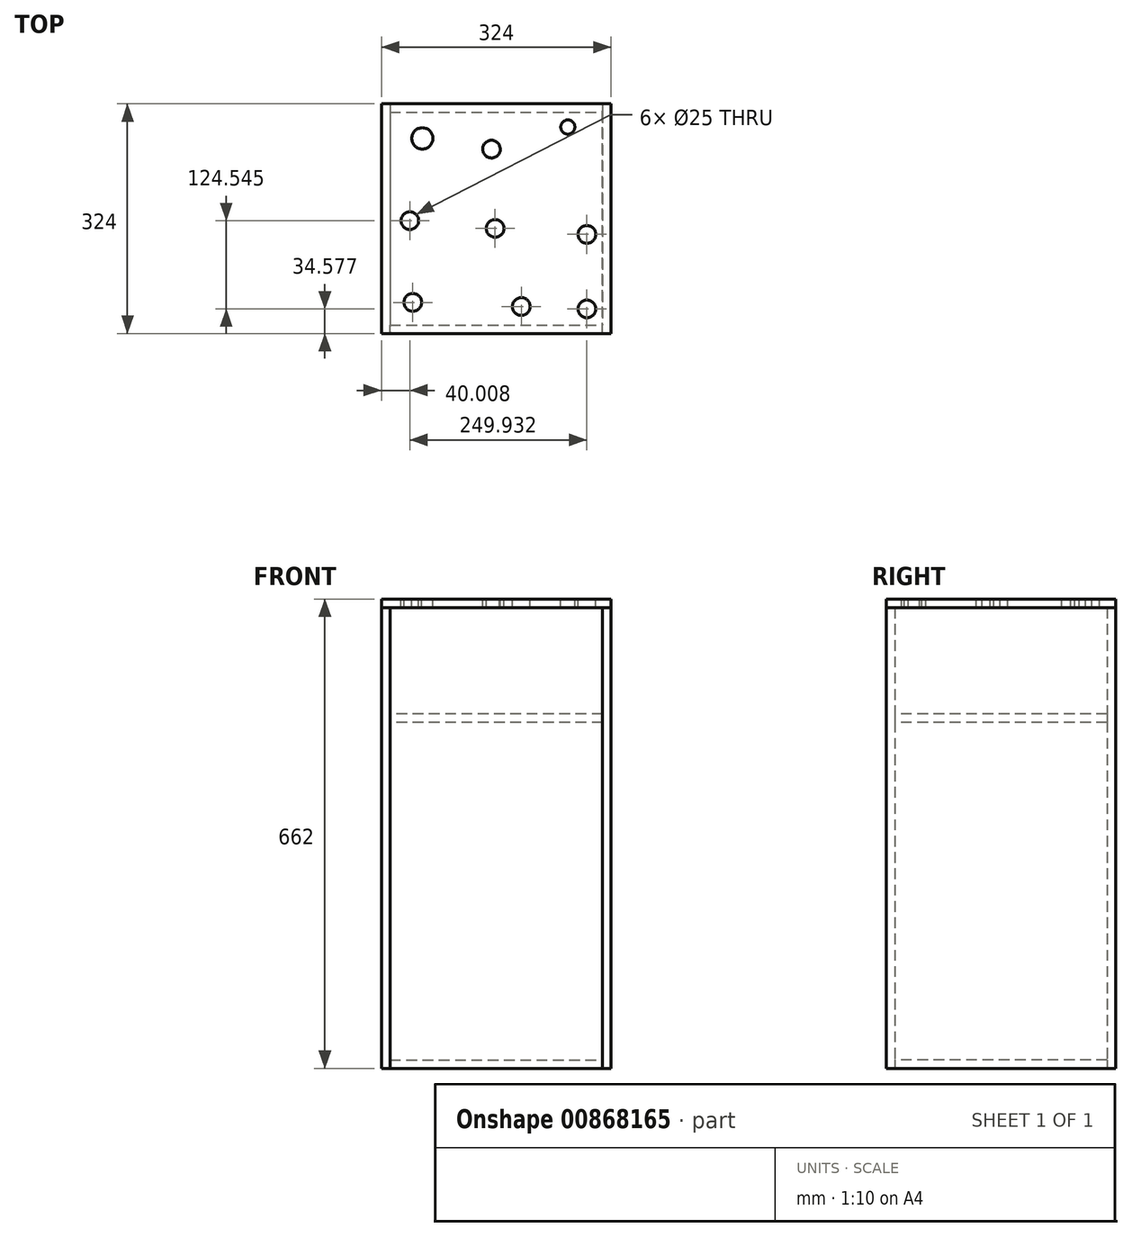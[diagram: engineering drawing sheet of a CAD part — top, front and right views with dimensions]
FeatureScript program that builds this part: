
annotation { "Feature Type Name" : "Feature", "Feature Type Description" : "" }
export const myFeature = defineFeature(function(context is Context, id is Id, definition is map)
    precondition{}
    {
        {
            var Q0;
            Q0=qCreatedBy(makeId("Top.planeOp"),FACE);
            var sketch = newSketch(context, id + "F0", { "sketchPlane" : qUnion([Q0])});
            skLineSegment(sketch, "E0.bottom", {"start": v(-158.95, 142.22) * mm, "end": v(141.05, 142.22) * mm});
            skLineSegment(sketch, "E0.top", {"start": v(-158.95, -157.78) * mm, "end": v(141.05, -157.78) * mm});
            skLineSegment(sketch, "E0.left", {"start": v(-158.95, 142.22) * mm, "end": v(-158.95, -157.78) * mm});
            skLineSegment(sketch, "E0.right", {"start": v(141.05, 142.22) * mm, "end": v(141.05, -157.78) * mm});
            skSolve(sketch);
        }
        {
            var Q0;
            Q0 = qSketchRegion(id + "F0", true);
            extrude(context, id + "F1", {"entities" : qUnion([Q0]), "depth" : 12 * mm, "offsetDistance" : 25 * mm});
        }
        {
            var Q0;
            Q0=makeQuery(id+"F1.opExtrude","SWEPT_FACE",FACE,{"disambiguationData":[OSD([sQuery(id+"F0.wireOp",EDGE,"E0.top")])]});
            var sketch = newSketch(context, id + "F2", { "sketchPlane" : qUnion([Q0])});
            skLineSegment(sketch, "E1.bottom", {"start": v(-158.95, 0) * mm, "end": v(141.05, 0) * mm});
            skLineSegment(sketch, "E1.top", {"start": v(-158.95, 650) * mm, "end": v(141.05, 650) * mm});
            skLineSegment(sketch, "E1.left", {"start": v(-158.95, 0) * mm, "end": v(-158.95, 650) * mm});
            skLineSegment(sketch, "E1.right", {"start": v(141.05, 0) * mm, "end": v(141.05, 650) * mm});
            skSolve(sketch);
        }
        {
            var Q0;
            Q0 = qSketchRegion(id + "F2", true);
            extrude(context, id + "F3", {"entities" : qUnion([Q0]), "depth" : 12 * mm, "offsetDistance" : 25 * mm});
        }
        {
            var Q0;
            Q0=makeQuery(id+"F1.opExtrude","SWEPT_FACE",FACE,{"disambiguationData":[OSD([sQuery(id+"F0.wireOp",EDGE,"E0.bottom")])]});
            var sketch = newSketch(context, id + "F4", { "sketchPlane" : qUnion([Q0])});
            skLineSegment(sketch, "E2.bottom", {"start": v(-141.05, 0) * mm, "end": v(158.95, 0) * mm});
            skLineSegment(sketch, "E2.top", {"start": v(-141.05, 650) * mm, "end": v(158.95, 650) * mm});
            skLineSegment(sketch, "E2.left", {"start": v(-141.05, 0) * mm, "end": v(-141.05, 650) * mm});
            skLineSegment(sketch, "E2.right", {"start": v(158.95, 0) * mm, "end": v(158.95, 650) * mm});
            skSolve(sketch);
        }
        {
            var Q0;
            Q0 = qSketchRegion(id + "F4", true);
            extrude(context, id + "F5", {"entities" : qUnion([Q0]), "depth" : 12 * mm, "offsetDistance" : 25 * mm});
        }
        {
            var Q0;
            Q0=makeQuery(id+"F3.opExtrude","CAP_FACE",FACE,{"disambiguationData":[OSD([sQuery(id+"F2.wireOp",EDGE,"E1.bottom"),sQuery(id+"F2.wireOp",EDGE,"E1.top"),sQuery(id+"F2.wireOp",EDGE,"E1.left"),sQuery(id+"F2.wireOp",EDGE,"E1.right")])],"isStart":true});
            var sketch = newSketch(context, id + "F6", { "sketchPlane" : qUnion([Q0])});
            skLineSegment(sketch, "E3.bottom", {"start": v(-141.05, 500) * mm, "end": v(158.95, 500) * mm});
            skLineSegment(sketch, "E3.top", {"start": v(-141.05, 488) * mm, "end": v(158.95, 488) * mm});
            skLineSegment(sketch, "E3.left", {"start": v(-141.05, 500) * mm, "end": v(-141.05, 488) * mm});
            skLineSegment(sketch, "E3.right", {"start": v(158.95, 500) * mm, "end": v(158.95, 488) * mm});
            skSolve(sketch);
        }
        {
            var Q0;
            Q0 = qSketchRegion(id + "F6", true);
            var Q1;
            Q1=makeQuery(id+"F5.opExtrude","CAP_FACE",FACE,{"disambiguationData":[OSD([sQuery(id+"F4.wireOp",EDGE,"E2.bottom"),sQuery(id+"F4.wireOp",EDGE,"E2.top"),sQuery(id+"F4.wireOp",EDGE,"E2.left"),sQuery(id+"F4.wireOp",EDGE,"E2.right")])],"isStart":true});
            extrude(context, id + "F7", {"entities" : qUnion([Q0]), "endBound" : BoundingType.UP_TO_SURFACE, "depth" : 25 * mm, "endBoundEntityFace" : qUnion([Q1]), "offsetDistance" : 25 * mm});
        }
        {
            var Q0;
            Q0=makeQuery(id+"F3.opExtrude","SWEPT_FACE",FACE,{"disambiguationData":[OSD([sQuery(id+"F2.wireOp",EDGE,"E1.right")])]});
            var sketch = newSketch(context, id + "F8", { "sketchPlane" : qUnion([Q0])});
            skLineSegment(sketch, "E4.bottom", {"start": v(-169.78, 0) * mm, "end": v(154.22, 0) * mm});
            skLineSegment(sketch, "E4.top", {"start": v(-169.78, 650) * mm, "end": v(154.22, 650) * mm});
            skLineSegment(sketch, "E4.left", {"start": v(-169.78, 0) * mm, "end": v(-169.78, 650) * mm});
            skLineSegment(sketch, "E4.right", {"start": v(154.22, 0) * mm, "end": v(154.22, 650) * mm});
            skSolve(sketch);
        }
        {
            var Q0;
            Q0 = qSketchRegion(id + "F8", true);
            extrude(context, id + "F9", {"entities" : qUnion([Q0]), "depth" : 12 * mm, "offsetDistance" : 25 * mm});
        }
        {
            var Q0;
            Q0=makeQuery(id+"F5.opExtrude","SWEPT_FACE",FACE,{"disambiguationData":[OSD([sQuery(id+"F4.wireOp",EDGE,"E2.right")])]});
            var sketch = newSketch(context, id + "F10", { "sketchPlane" : qUnion([Q0])});
            skLineSegment(sketch, "E5.bottom", {"start": v(-154.22, 650) * mm, "end": v(169.78, 650) * mm});
            skLineSegment(sketch, "E5.top", {"start": v(-154.22, 0) * mm, "end": v(169.78, 0) * mm});
            skLineSegment(sketch, "E5.left", {"start": v(-154.22, 650) * mm, "end": v(-154.22, 0) * mm});
            skLineSegment(sketch, "E5.right", {"start": v(169.78, 650) * mm, "end": v(169.78, 0) * mm});
            skSolve(sketch);
        }
        {
            var Q0;
            Q0 = qSketchRegion(id + "F10", true);
            extrude(context, id + "F11", {"entities" : qUnion([Q0]), "depth" : 12 * mm, "offsetDistance" : 25 * mm});
        }
        {
            var Q0;
            Q0=makeQuery(id+"F9.opExtrude","SWEPT_FACE",FACE,{"disambiguationData":[OSD([sQuery(id+"F8.wireOp",EDGE,"E4.top")])]});
            var sketch = newSketch(context, id + "F12", { "sketchPlane" : qUnion([Q0])});
            skLineSegment(sketch, "E6.bottom", {"start": v(153.05, -169.78) * mm, "end": v(-170.95, -169.78) * mm});
            skLineSegment(sketch, "E6.top", {"start": v(153.05, 154.22) * mm, "end": v(-170.95, 154.22) * mm});
            skLineSegment(sketch, "E6.left", {"start": v(153.05, -169.78) * mm, "end": v(153.05, 154.22) * mm});
            skLineSegment(sketch, "E6.right", {"start": v(-170.95, -169.78) * mm, "end": v(-170.95, 154.22) * mm});
            skSolve(sketch);
        }
        {
            var Q0;
            Q0 = qSketchRegion(id + "F12", true);
            extrude(context, id + "F13", {"entities" : qUnion([Q0]), "depth" : 12 * mm, "offsetDistance" : 25 * mm});
        }
        {
            var Q0;
            Q0=makeQuery(id+"F13.opExtrude","CAP_FACE",FACE,{"disambiguationData":[OSD([sQuery(id+"F12.wireOp",EDGE,"E6.bottom"),sQuery(id+"F12.wireOp",EDGE,"E6.top"),sQuery(id+"F12.wireOp",EDGE,"E6.left"),sQuery(id+"F12.wireOp",EDGE,"E6.right")])],"isStart":false});
            var sketch = newSketch(context, id + "F14", { "sketchPlane" : qUnion([Q0])});
            skCircle(sketch, "E7", {"center": v(-126.73, -125.95) * mm, "radius": 12.5 * mm});
            skCircle(sketch, "E8", {"center": v(-113.27, 105.47) * mm, "radius": 15 * mm});
            skCircle(sketch, "E9", {"center": v(-15.65, 90.33) * mm, "radius": 12.5 * mm});
            skCircle(sketch, "E10", {"center": v(92.06, 121.46) * mm, "radius": 10 * mm});
            skCircle(sketch, "E11", {"center": v(-130.94, -10.66) * mm, "radius": 12.5 * mm});
            skCircle(sketch, "E12", {"center": v(-10.6, -21.6) * mm, "radius": 12.5 * mm});
            skCircle(sketch, "E13", {"center": v(118.99, -30.01) * mm, "radius": 12.5 * mm});
            skCircle(sketch, "E14", {"center": v(26.42, -131.84) * mm, "radius": 12.5 * mm});
            skCircle(sketch, "E15", {"center": v(118.99, -135.2) * mm, "radius": 12.5 * mm});
            skCircle(sketch, "E16", {"center": v(-15.65, 90.33) * mm, "radius": 60 * mm});
            skCircle(sketch, "E17", {"center": v(92.06, 121.46) * mm, "radius": 100 * mm});
            skCircle(sketch, "E18", {"center": v(-113.27, 105.47) * mm, "radius": 100 * mm});
            skCircle(sketch, "E19", {"center": v(-130.94, -10.66) * mm, "radius": 60 * mm});
            skCircle(sketch, "E20", {"center": v(-10.6, -21.6) * mm, "radius": 60 * mm});
            skCircle(sketch, "E21", {"center": v(118.99, -30.01) * mm, "radius": 60 * mm});
            skCircle(sketch, "E22", {"center": v(118.99, -135.2) * mm, "radius": 60 * mm});
            skCircle(sketch, "E23", {"center": v(26.42, -131.84) * mm, "radius": 60 * mm});
            skCircle(sketch, "E24", {"center": v(-126.73, -125.95) * mm, "radius": 100 * mm});
            skSolve(sketch);
        }
        {
            var Q0;
            Q0=makeQuery(id+"F14.imprint","IMPRINT",FACE,{"disambiguationData":[TD([[makeQuery(id+"F14.imprint","IMPRINT",EDGE,{"derivedFrom":sQuery(id+"F14.wireOp",EDGE,"E8")}),1.0]])]});
            var Q1;
            {var subQ0=sQuery(id+"F14.wireOp",EDGE,"E17");var subQ1=sQuery(id+"F14.wireOp",EDGE,"E9");var subQ2=makeQuery(id+"F14.imprint","INTERSECT",VERTEX,{"disambiguationData":[OD(0.0)],"derivedFrom":[subQ1,subQ0]});Q1=makeQuery(id+"F14.imprint","IMPRINT",FACE,{"disambiguationData":[TD([[makeQuery(id+"F14.imprint","IMPRINT",EDGE,{"disambiguationData":[TD([[subQ2,-1.0]])],"derivedFrom":subQ1}),1.0]])]});}
            var Q2;
            {var subQ0=sQuery(id+"F14.wireOp",EDGE,"E18");var subQ1=sQuery(id+"F14.wireOp",EDGE,"E9");var subQ2=makeQuery(id+"F14.imprint","INTERSECT",VERTEX,{"disambiguationData":[OD(0.0)],"derivedFrom":[subQ1,subQ0]});Q2=makeQuery(id+"F14.imprint","IMPRINT",FACE,{"disambiguationData":[TD([[makeQuery(id+"F14.imprint","IMPRINT",EDGE,{"disambiguationData":[TD([[subQ2,-1.0]])],"derivedFrom":subQ1}),1.0]])]});}
            var Q3;
            Q3=makeQuery(id+"F14.imprint","IMPRINT",FACE,{"disambiguationData":[TD([[makeQuery(id+"F14.imprint","IMPRINT",EDGE,{"derivedFrom":sQuery(id+"F14.wireOp",EDGE,"E10")}),1.0]])]});
            var Q4;
            Q4=makeQuery(id+"F14.imprint","IMPRINT",FACE,{"disambiguationData":[TD([[makeQuery(id+"F14.imprint","IMPRINT",EDGE,{"derivedFrom":sQuery(id+"F14.wireOp",EDGE,"E12")}),1.0]])]});
            var Q5;
            Q5=makeQuery(id+"F14.imprint","IMPRINT",FACE,{"disambiguationData":[TD([[makeQuery(id+"F14.imprint","IMPRINT",EDGE,{"derivedFrom":sQuery(id+"F14.wireOp",EDGE,"E11")}),1.0]])]});
            var Q6;
            Q6=makeQuery(id+"F14.imprint","IMPRINT",FACE,{"disambiguationData":[TD([[makeQuery(id+"F14.imprint","IMPRINT",EDGE,{"derivedFrom":sQuery(id+"F14.wireOp",EDGE,"E13")}),1.0]])]});
            var Q7;
            Q7=makeQuery(id+"F14.imprint","IMPRINT",FACE,{"disambiguationData":[TD([[makeQuery(id+"F14.imprint","IMPRINT",EDGE,{"derivedFrom":sQuery(id+"F14.wireOp",EDGE,"E15")}),1.0]])]});
            var Q8;
            Q8=makeQuery(id+"F14.imprint","IMPRINT",FACE,{"disambiguationData":[TD([[makeQuery(id+"F14.imprint","IMPRINT",EDGE,{"derivedFrom":sQuery(id+"F14.wireOp",EDGE,"E14")}),1.0]])]});
            var Q9;
            Q9=makeQuery(id+"F14.imprint","IMPRINT",FACE,{"disambiguationData":[TD([[makeQuery(id+"F14.imprint","IMPRINT",EDGE,{"derivedFrom":sQuery(id+"F14.wireOp",EDGE,"E7")}),1.0]])]});
            extrude(context, id + "F15", {"entities" : qUnion([Q0, Q1, Q2, Q3, Q4, Q5, Q6, Q7, Q8, Q9]), "operationType" : NewBodyOperationType.REMOVE, "oppositeDirection" : true, "depth" : 25 * mm, "offsetDistance" : 25 * mm});
        }
    });
